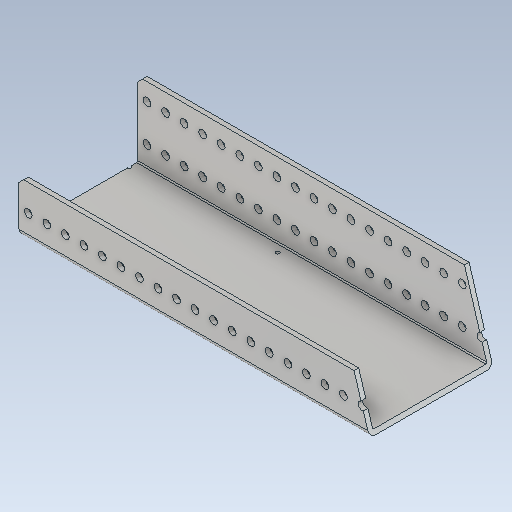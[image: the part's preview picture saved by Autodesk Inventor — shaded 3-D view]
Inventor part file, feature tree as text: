
AUTODESK INVENTOR PART (.ipt)
format: ipt  version: 2020 (Build 240168000, 168)  size: 377,856 bytes
history: native  units: in
note: dims shown in document units (in); Inventor stores cm internally (conversion verified against a paired STEP export)
features: extrude x1, sketch x1, other x1
ambient origin geometry x8: Origin, YZ Plane, XZ Plane, XY Plane, X Axis, Y Axis, Z Axis, Center Point
bodies: Solid1 (feature_tree)
feature tree (3):
  extrude  "Extrusion1"  TaperAngle=0.0deg  [1 undecoded]
  sketch  "Sketch1"  dims[d0=9.5in d1=0.0in d2=0.0in]
  other  "_AM14U3 End Sheet Rev1_-_LPattern4_"
note: 1 required parameter value undecoded (feature->parameter linkage not recoverable at this tier; creation-order binding heuristic only, values carry confidence <= 0.55)
